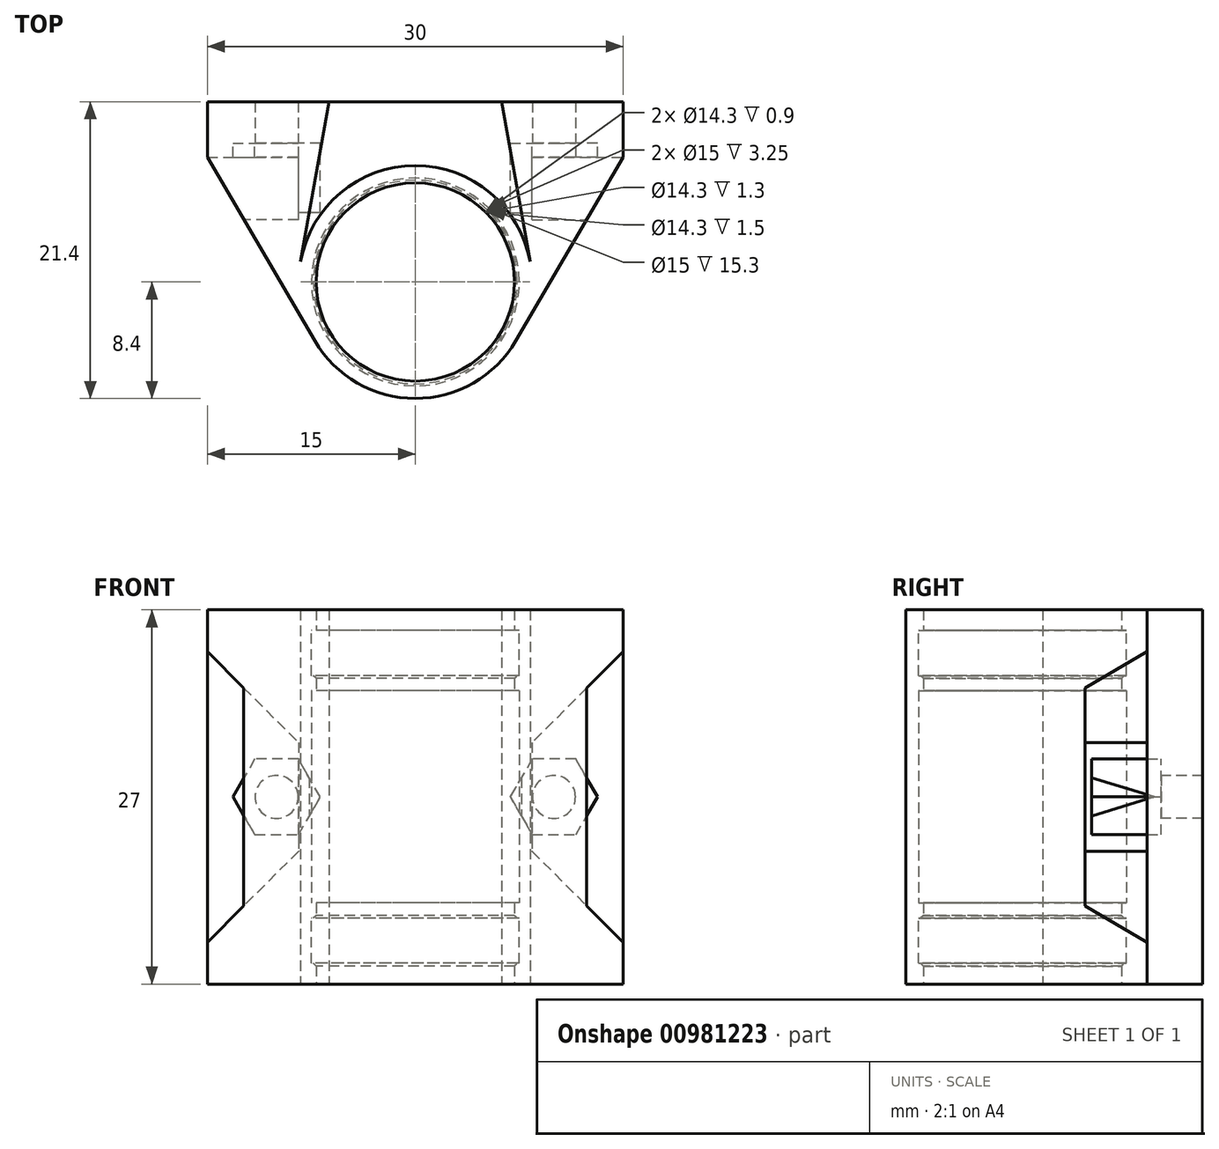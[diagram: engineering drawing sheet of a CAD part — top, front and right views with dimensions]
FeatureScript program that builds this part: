
annotation { "Feature Type Name" : "Feature", "Feature Type Description" : "" }
export const myFeature = defineFeature(function(context is Context, id is Id, definition is map)
    precondition{}
    {
        {
            var Q0;
            Q0=qCreatedBy(makeId("Top.planeOp"),FACE);
            var sketch = newSketch(context, id + "F0", { "sketchPlane" : qUnion([Q0])});
            skCircle(sketch, "E0", {"center": v(0, 0) * mm, "radius": 7.5 * mm});
            skLineSegment(sketch, "E1.top", {"start": v(-15, 9) * mm, "end": v(15, 9) * mm});
            skPoint(sketch, "E2", {"position": v(0, 9) * mm});
            skCircle(sketch, "E3", {"center": v(0, 0) * mm, "radius": 8.4 * mm});
            skCircle(sketch, "E4", {"center": v(0, 0) * mm, "radius": 7.15 * mm});
            skLineSegment(sketch, "E5", {"start": v(-8.27, 1.46) * mm, "end": v(-6.24, 13) * mm});
            skLineSegment(sketch, "E6", {"start": v(8.27, 1.46) * mm, "end": v(6.24, 13) * mm});
            skLineSegment(sketch, "E7", {"start": v(-15, 9) * mm, "end": v(-15, 13) * mm});
            skLineSegment(sketch, "E8", {"start": v(-15, 13) * mm, "end": v(15, 13) * mm});
            skLineSegment(sketch, "E9", {"start": v(15, 13) * mm, "end": v(15, 9) * mm});
            skLineSegment(sketch, "E10", {"start": v(-15, 9) * mm, "end": v(-7.25, -4.24) * mm});
            skLineSegment(sketch, "E11", {"start": v(15, 9) * mm, "end": v(7.25, -4.24) * mm});
            skLineSegment(sketch, "E12", {"start": v(9.73, 0) * mm, "end": v(-9.73, 0) * mm});
            skSolve(sketch);
        }
        {
            var Q0;
            {var subQ0=sQuery(id+"F0.wireOp",EDGE,"E5");var subQ1=sQuery(id+"F0.wireOp",EDGE,"E1.top");var subQ2=makeQuery(id+"F0.imprint","INTERSECT",VERTEX,{"derivedFrom":[subQ1,subQ0]});Q0=makeQuery(id+"F0.imprint","IMPRINT",FACE,{"disambiguationData":[TD([[makeQuery(id+"F0.imprint","IMPRINT",EDGE,{"disambiguationData":[TD([[subQ2,-1.0]])],"derivedFrom":subQ1}),1.0]])]});}
            var Q1;
            {var subQ0=sQuery(id+"F0.wireOp",EDGE,"E5");var subQ1=sQuery(id+"F0.wireOp",EDGE,"E1.top");var subQ2=makeQuery(id+"F0.imprint","INTERSECT",VERTEX,{"derivedFrom":[subQ1,subQ0]});Q1=makeQuery(id+"F0.imprint","IMPRINT",FACE,{"disambiguationData":[TD([[makeQuery(id+"F0.imprint","IMPRINT",EDGE,{"disambiguationData":[TD([[subQ2,-1.0]])],"derivedFrom":subQ1}),-1.0]])]});}
            var Q2;
            {var subQ2=sQuery(id+"F0.wireOp",EDGE,"E12");var subQ6=sQuery(id+"F0.wireOp",EDGE,"E0");var subQ7=makeQuery(id+"F0.imprint","INTERSECT",VERTEX,{"disambiguationData":[OD(0.0)],"derivedFrom":[subQ6,subQ2]});Q2=makeQuery(id+"F0.imprint","IMPRINT",FACE,{"disambiguationData":[TD([[makeQuery(id+"F0.imprint","IMPRINT",EDGE,{"disambiguationData":[TD([[subQ7,-1.0]])],"derivedFrom":subQ6}),-1.0]])]});}
            var Q3;
            {var subQ0=sQuery(id+"F0.wireOp",EDGE,"E12");var subQ1=sQuery(id+"F0.wireOp",EDGE,"E0");var subQ2=makeQuery(id+"F0.imprint","INTERSECT",VERTEX,{"disambiguationData":[OD(0.0)],"derivedFrom":[subQ1,subQ0]});Q3=makeQuery(id+"F0.imprint","IMPRINT",FACE,{"disambiguationData":[TD([[makeQuery(id+"F0.imprint","IMPRINT",EDGE,{"disambiguationData":[TD([[subQ2,-1.0]])],"derivedFrom":subQ1}),1.0]])]});}
            extrude(context, id + "F1", {"entities" : qUnion([Q0, Q1, Q2, Q3]), "endBound" : BoundingType.SYMMETRIC, "depth" : 27 * mm, "offsetDistance" : 25 * mm});
        }
        {
            var Q0;
            {var subQ3=sQuery(id+"F0.wireOp",EDGE,"E5");var subQ5=sQuery(id+"F0.wireOp",EDGE,"2ioF6rcV-CoDT-8IXQ-bcVH-CRvURSwV3O7U");var subQ6=makeQuery(id+"F0.imprint","INTERSECT",VERTEX,{"derivedFrom":[subQ3,subQ5]});Q0=makeQuery(id+"F0.imprint","IMPRINT",FACE,{"disambiguationData":[TD([[makeQuery(id+"F0.imprint","IMPRINT",EDGE,{"disambiguationData":[TD([[subQ6,1.0]])],"derivedFrom":subQ3}),1.0]])]});}
            var Q1;
            {var subQ1=sQuery(id+"F0.wireOp",EDGE,"E1.top");var subQ3=sQuery(id+"F0.wireOp",EDGE,"E5");var subQ4=makeQuery(id+"F0.imprint","INTERSECT",VERTEX,{"derivedFrom":[subQ1,subQ3]});Q1=makeQuery(id+"F0.imprint","IMPRINT",FACE,{"disambiguationData":[TD([[makeQuery(id+"F0.imprint","IMPRINT",EDGE,{"disambiguationData":[TD([[subQ4,1.0]])],"derivedFrom":subQ1}),-1.0]])]});}
            var Q2;
            {var subQ0=sQuery(id+"F0.wireOp",EDGE,"E12");var subQ6=sQuery(id+"F0.wireOp",EDGE,"E0");var subQ8=makeQuery(id+"F0.imprint","INTERSECT",VERTEX,{"disambiguationData":[OD(0.0)],"derivedFrom":[subQ6,subQ0]});Q2=makeQuery(id+"F0.imprint","IMPRINT",FACE,{"disambiguationData":[TD([[makeQuery(id+"F0.imprint","IMPRINT",EDGE,{"disambiguationData":[TD([[subQ8,1.0]])],"derivedFrom":subQ6}),-1.0]])]});}
            var Q3;
            {var subQ1=sQuery(id+"F0.wireOp",EDGE,"E3");var subQ3=sQuery(id+"F0.wireOp",EDGE,"E10");var subQ4=makeQuery(id+"F0.imprint","INTERSECT",VERTEX,{"derivedFrom":[subQ1,subQ3]});Q3=makeQuery(id+"F0.imprint","IMPRINT",FACE,{"disambiguationData":[TD([[makeQuery(id+"F0.imprint","IMPRINT",EDGE,{"disambiguationData":[TD([[subQ4,1.0]])],"derivedFrom":subQ3}),1.0]])]});}
            var Q4;
            {var subQ1=sQuery(id+"F0.wireOp",EDGE,"E3");var subQ3=sQuery(id+"F0.wireOp",EDGE,"E11");var subQ4=makeQuery(id+"F0.imprint","INTERSECT",VERTEX,{"derivedFrom":[subQ1,subQ3]});Q4=makeQuery(id+"F0.imprint","IMPRINT",FACE,{"disambiguationData":[TD([[makeQuery(id+"F0.imprint","IMPRINT",EDGE,{"disambiguationData":[TD([[subQ4,1.0]])],"derivedFrom":subQ3}),-1.0]])]});}
            var Q5;
            {var subQ1=sQuery(id+"F0.wireOp",EDGE,"E1.top");var subQ3=sQuery(id+"F0.wireOp",EDGE,"E6");var subQ4=makeQuery(id+"F0.imprint","INTERSECT",VERTEX,{"derivedFrom":[subQ1,subQ3]});Q5=makeQuery(id+"F0.imprint","IMPRINT",FACE,{"disambiguationData":[TD([[makeQuery(id+"F0.imprint","IMPRINT",EDGE,{"disambiguationData":[TD([[subQ4,-1.0]])],"derivedFrom":subQ1}),-1.0]])]});}
            var Q6;
            {var subQ3=sQuery(id+"F0.wireOp",EDGE,"E6");var subQ5=sQuery(id+"F0.wireOp",EDGE,"2ioF6rcV-CoDT-8IXQ-bcVH-CRvURSwV3O7U");var subQ6=makeQuery(id+"F0.imprint","INTERSECT",VERTEX,{"derivedFrom":[subQ3,subQ5]});Q6=makeQuery(id+"F0.imprint","IMPRINT",FACE,{"disambiguationData":[TD([[makeQuery(id+"F0.imprint","IMPRINT",EDGE,{"disambiguationData":[TD([[subQ6,1.0]])],"derivedFrom":subQ3}),-1.0]])]});}
            var Q7;
            {var subQ0=sQuery(id+"F0.wireOp",EDGE,"E12");var subQ1=sQuery(id+"F0.wireOp",EDGE,"E0");var subQ2=makeQuery(id+"F0.imprint","INTERSECT",VERTEX,{"disambiguationData":[OD(0.0)],"derivedFrom":[subQ1,subQ0]});Q7=makeQuery(id+"F0.imprint","IMPRINT",FACE,{"disambiguationData":[TD([[makeQuery(id+"F0.imprint","IMPRINT",EDGE,{"disambiguationData":[TD([[subQ2,1.0]])],"derivedFrom":subQ1}),1.0]])]});}
            extrude(context, id + "F2", {"entities" : qUnion([Q0, Q1, Q2, Q3, Q4, Q5, Q6, Q7]), "endBound" : BoundingType.SYMMETRIC, "depth" : 27 * mm, "offsetDistance" : 25 * mm});
        }
        {
            var Q0;
            {var subQ0=sQuery(id+"F0.wireOp",EDGE,"E12");var subQ1=sQuery(id+"F0.wireOp",EDGE,"E0");var subQ2=makeQuery(id+"F0.imprint","INTERSECT",VERTEX,{"disambiguationData":[OD(0.0)],"derivedFrom":[subQ1,subQ0]});Q0=makeQuery(id+"F0.imprint","IMPRINT",FACE,{"disambiguationData":[TD([[makeQuery(id+"F0.imprint","IMPRINT",EDGE,{"disambiguationData":[TD([[subQ2,-1.0]])],"derivedFrom":subQ1}),1.0]])]});}
            var Q1;
            {var subQ0=sQuery(id+"F0.wireOp",EDGE,"E12");var subQ1=sQuery(id+"F0.wireOp",EDGE,"E0");var subQ2=makeQuery(id+"F0.imprint","INTERSECT",VERTEX,{"disambiguationData":[OD(0.0)],"derivedFrom":[subQ1,subQ0]});Q1=makeQuery(id+"F0.imprint","IMPRINT",FACE,{"disambiguationData":[TD([[makeQuery(id+"F0.imprint","IMPRINT",EDGE,{"disambiguationData":[TD([[subQ2,1.0]])],"derivedFrom":subQ1}),1.0]])]});}
            extrude(context, id + "F3", {"entities" : qUnion([Q0, Q1]), "operationType" : NewBodyOperationType.REMOVE, "endBound" : BoundingType.SYMMETRIC, "oppositeDirection" : true, "depth" : 24 * mm, "offsetDistance" : 25 * mm});
        }
        {
            var Q0;
            {var subQ0=sQuery(id+"F0.wireOp",EDGE,"E12");var subQ1=sQuery(id+"F0.wireOp",EDGE,"E0");var subQ2=makeQuery(id+"F0.imprint","INTERSECT",VERTEX,{"disambiguationData":[OD(0.0)],"derivedFrom":[subQ1,subQ0]});Q0=makeQuery(id+"F0.imprint","IMPRINT",FACE,{"disambiguationData":[TD([[makeQuery(id+"F0.imprint","IMPRINT",EDGE,{"disambiguationData":[TD([[subQ2,-1.0]])],"derivedFrom":subQ1}),1.0]])]});}
            extrude(context, id + "F4", {"entities" : qUnion([Q0]), "operationType" : NewBodyOperationType.ADD, "endBound" : BoundingType.SYMMETRIC, "depth" : 17.5 * mm, "offsetDistance" : 25 * mm});
        }
        {
            var Q0;
            {var subQ0=sQuery(id+"F0.wireOp",EDGE,"E12");var subQ1=sQuery(id+"F0.wireOp",EDGE,"E0");var subQ2=makeQuery(id+"F0.imprint","INTERSECT",VERTEX,{"disambiguationData":[OD(0.0)],"derivedFrom":[subQ1,subQ0]});Q0=makeQuery(id+"F0.imprint","IMPRINT",FACE,{"disambiguationData":[TD([[makeQuery(id+"F0.imprint","IMPRINT",EDGE,{"disambiguationData":[TD([[subQ2,1.0]])],"derivedFrom":subQ1}),1.0]])]});}
            extrude(context, id + "F5", {"entities" : qUnion([Q0]), "operationType" : NewBodyOperationType.ADD, "endBound" : BoundingType.SYMMETRIC, "depth" : 17.5 * mm, "offsetDistance" : 25 * mm});
        }
        {
            var Q0;
            {var subQ0=sQuery(id+"F0.wireOp",EDGE,"E12");var subQ1=sQuery(id+"F0.wireOp",EDGE,"E0");var subQ2=makeQuery(id+"F0.imprint","INTERSECT",VERTEX,{"disambiguationData":[OD(0.0)],"derivedFrom":[subQ1,subQ0]});Q0=makeQuery(id+"F0.imprint","IMPRINT",FACE,{"disambiguationData":[TD([[makeQuery(id+"F0.imprint","IMPRINT",EDGE,{"disambiguationData":[TD([[subQ2,-1.0]])],"derivedFrom":subQ1}),1.0]])]});}
            var Q1;
            {var subQ0=sQuery(id+"F0.wireOp",EDGE,"E12");var subQ1=sQuery(id+"F0.wireOp",EDGE,"E0");var subQ2=makeQuery(id+"F0.imprint","INTERSECT",VERTEX,{"disambiguationData":[OD(0.0)],"derivedFrom":[subQ1,subQ0]});Q1=makeQuery(id+"F0.imprint","IMPRINT",FACE,{"disambiguationData":[TD([[makeQuery(id+"F0.imprint","IMPRINT",EDGE,{"disambiguationData":[TD([[subQ2,1.0]])],"derivedFrom":subQ1}),1.0]])]});}
            var Q2;
            Q2=makeQuery(id+"F4.opExtrude","CAP_FACE",FACE,{"disambiguationData":[OSD([sQuery(id+"F0.wireOp",EDGE,"E0"),sQuery(id+"F0.wireOp",EDGE,"E4"),sQuery(id+"F0.wireOp",EDGE,"OyqxnQTL-80hJ-Tre8-0LPI-5BT4BykeZ9OB"),sQuery(id+"F0.wireOp",EDGE,"toQEOSAH-RIUy-FKcM-AJDC-1LW4buzCWPbQ")])],"isStart":false});
            var Q3;
            Q3=makeQuery(id+"F4.opExtrude","CAP_FACE",FACE,{"disambiguationData":[OSD([sQuery(id+"F0.wireOp",EDGE,"E0"),sQuery(id+"F0.wireOp",EDGE,"E4"),sQuery(id+"F0.wireOp",EDGE,"OyqxnQTL-80hJ-Tre8-0LPI-5BT4BykeZ9OB"),sQuery(id+"F0.wireOp",EDGE,"toQEOSAH-RIUy-FKcM-AJDC-1LW4buzCWPbQ")])],"isStart":true});
            extrude(context, id + "F6", {"entities" : qUnion([Q0, Q1]), "operationType" : NewBodyOperationType.REMOVE, "endBound" : BoundingType.UP_TO_SURFACE, "depth" : 15 * mm, "endBoundEntityFace" : qUnion([Q2]), "hasOffset" : true, "offsetDistance" : 1.1 * mm, "hasSecondDirection" : true, "secondDirectionBound" : SecondDirectionBoundingType.UP_TO_SURFACE, "secondDirectionOppositeDirection" : true, "secondDirectionDepth" : 25 * mm, "secondDirectionBoundEntityFace" : qUnion([Q3]), "hasSecondDirectionOffset" : true, "secondDirectionOffsetDistance" : 1.1 * mm});
        }
        {
            var Q0;
            Q0=makeQuery(id+"F1.opExtrude","SWEPT_FACE",FACE,{"disambiguationData":[OSD([sQuery(id+"F0.wireOp",EDGE,"E8")])]});
            cPlane(context, id + "F7", {"entities" : qUnion([Q0]), "cplaneType" : CPlaneType.OFFSET, "offset" : 4 * mm, "oppositeDirection" : true, "width" : 150 * mm, "height" : 150 * mm});
        }
        {
            var Q0;
            Q0=qCreatedBy(id+"F7.planeOp",FACE);
            var sketch = newSketch(context, id + "F8", { "sketchPlane" : qUnion([Q0])});
            skCircle(sketch, "E13", {"center": v(-10, 0) * mm, "radius": 1.55 * mm});
            skCircle(sketch, "E14", {"center": v(10, 0) * mm, "radius": 1.55 * mm});
            skCircle(sketch, "E15.cCircle", {"center": v(-10, 0) * mm, "radius": 3.15 * mm, "construction": true});
            skLineSegment(sketch, "E15.0", {"start": v(-6.85, 0) * mm, "end": v(-8.43, -2.73) * mm});
            skLineSegment(sketch, "E15.1", {"start": v(-8.43, -2.73) * mm, "end": v(-11.58, -2.73) * mm});
            skLineSegment(sketch, "E15.2", {"start": v(-11.58, -2.73) * mm, "end": v(-13.15, 0) * mm});
            skLineSegment(sketch, "E15.3", {"start": v(-13.15, 0) * mm, "end": v(-11.58, 2.73) * mm});
            skLineSegment(sketch, "E15.4", {"start": v(-11.58, 2.73) * mm, "end": v(-8.43, 2.73) * mm});
            skLineSegment(sketch, "E15.5", {"start": v(-8.43, 2.73) * mm, "end": v(-6.85, 0) * mm});
            skCircle(sketch, "E16.cCircle", {"center": v(10, 0) * mm, "radius": 3.15 * mm, "construction": true});
            skLineSegment(sketch, "E16.0", {"start": v(6.85, 0) * mm, "end": v(8.43, 2.73) * mm});
            skLineSegment(sketch, "E16.1", {"start": v(8.43, 2.73) * mm, "end": v(11.58, 2.73) * mm});
            skLineSegment(sketch, "E16.2", {"start": v(11.58, 2.73) * mm, "end": v(13.15, 0) * mm});
            skLineSegment(sketch, "E16.3", {"start": v(13.15, 0) * mm, "end": v(11.58, -2.73) * mm});
            skLineSegment(sketch, "E16.4", {"start": v(11.58, -2.73) * mm, "end": v(8.43, -2.73) * mm});
            skLineSegment(sketch, "E16.5", {"start": v(8.43, -2.73) * mm, "end": v(6.85, 0) * mm});
            skLineSegment(sketch, "E17", {"start": v(-15, -10.5) * mm, "end": v(-15, 10.5) * mm});
            skLineSegment(sketch, "E18", {"start": v(-15, 10.5) * mm, "end": v(-8.43, 3.92) * mm});
            skLineSegment(sketch, "E19", {"start": v(-8.43, 3.92) * mm, "end": v(-8.43, -3.92) * mm});
            skLineSegment(sketch, "E20", {"start": v(-8.43, -3.92) * mm, "end": v(-15, -10.5) * mm});
            skLineSegment(sketch, "E21", {"start": v(15, 10.5) * mm, "end": v(8.43, 3.92) * mm});
            skLineSegment(sketch, "E22", {"start": v(8.43, 3.92) * mm, "end": v(8.43, -3.92) * mm});
            skLineSegment(sketch, "E23", {"start": v(8.43, -3.92) * mm, "end": v(15, -10.5) * mm});
            skLineSegment(sketch, "E24", {"start": v(15, -10.5) * mm, "end": v(15, 10.5) * mm});
            skPoint(sketch, "E25", {"position": v(-15, 0) * mm});
            skSolve(sketch);
        }
        {
            var Q0;
            {var subQ4=sQuery(id+"F8.wireOp",EDGE,"E15.2");Q0=makeQuery(id+"F8.imprint","IMPRINT",FACE,{"disambiguationData":[TD([[makeQuery(id+"F8.imprint","IMPRINT",EDGE,{"derivedFrom":subQ4}),1.0]])]});}
            var Q1;
            {var subQ5=sQuery(id+"F8.wireOp",EDGE,"E16.2");Q1=makeQuery(id+"F8.imprint","IMPRINT",FACE,{"disambiguationData":[TD([[makeQuery(id+"F8.imprint","IMPRINT",EDGE,{"derivedFrom":subQ5}),1.0]])]});}
            var Q2;
            {var subQ1=sQuery(id+"F8.wireOp",EDGE,"E16.2");Q2=makeQuery(id+"F8.imprint","IMPRINT",FACE,{"disambiguationData":[TD([[makeQuery(id+"F8.imprint","IMPRINT",EDGE,{"derivedFrom":subQ1}),-1.0]])]});}
            var Q3;
            {var subQ0=sQuery(id+"F8.wireOp",EDGE,"E22");var subQ1=sQuery(id+"F8.wireOp",EDGE,"E14");var subQ2=makeQuery(id+"F8.imprint","INTERSECT",VERTEX,{"disambiguationData":[OD(0.0)],"derivedFrom":[subQ1,subQ0]});Q3=makeQuery(id+"F8.imprint","IMPRINT",FACE,{"disambiguationData":[TD([[makeQuery(id+"F8.imprint","IMPRINT",EDGE,{"disambiguationData":[TD([[subQ2,1.0]])],"derivedFrom":subQ1}),1.0]])]});}
            var Q4;
            {var subQ1=sQuery(id+"F8.wireOp",EDGE,"E15.2");Q4=makeQuery(id+"F8.imprint","IMPRINT",FACE,{"disambiguationData":[TD([[makeQuery(id+"F8.imprint","IMPRINT",EDGE,{"derivedFrom":subQ1}),-1.0]])]});}
            var Q5;
            {var subQ0=sQuery(id+"F8.wireOp",EDGE,"E19");var subQ1=sQuery(id+"F8.wireOp",EDGE,"E13");var subQ2=makeQuery(id+"F8.imprint","INTERSECT",VERTEX,{"disambiguationData":[OD(0.0)],"derivedFrom":[subQ1,subQ0]});Q5=makeQuery(id+"F8.imprint","IMPRINT",FACE,{"disambiguationData":[TD([[makeQuery(id+"F8.imprint","IMPRINT",EDGE,{"disambiguationData":[TD([[subQ2,-1.0]])],"derivedFrom":subQ1}),1.0]])]});}
            extrude(context, id + "F9", {"entities" : qUnion([Q0, Q1, Q2, Q3, Q4, Q5]), "operationType" : NewBodyOperationType.REMOVE, "oppositeDirection" : true, "depth" : 4.5 * mm, "offsetDistance" : 25 * mm});
        }
        {
            var Q0;
            {var subQ1=sQuery(id+"F8.wireOp",EDGE,"E15.2");Q0=makeQuery(id+"F8.imprint","IMPRINT",FACE,{"disambiguationData":[TD([[makeQuery(id+"F8.imprint","IMPRINT",EDGE,{"derivedFrom":subQ1}),-1.0]])]});}
            var Q1;
            {var subQ5=sQuery(id+"F8.wireOp",EDGE,"E15.0");Q1=makeQuery(id+"F8.imprint","IMPRINT",FACE,{"disambiguationData":[TD([[makeQuery(id+"F8.imprint","IMPRINT",EDGE,{"derivedFrom":subQ5}),-1.0]])]});}
            var Q2;
            {var subQ0=sQuery(id+"F8.wireOp",EDGE,"E19");var subQ1=sQuery(id+"F8.wireOp",EDGE,"E13");var subQ2=makeQuery(id+"F8.imprint","INTERSECT",VERTEX,{"disambiguationData":[OD(0.0)],"derivedFrom":[subQ1,subQ0]});Q2=makeQuery(id+"F8.imprint","IMPRINT",FACE,{"disambiguationData":[TD([[makeQuery(id+"F8.imprint","IMPRINT",EDGE,{"disambiguationData":[TD([[subQ2,1.0]])],"derivedFrom":subQ1}),1.0]])]});}
            var Q3;
            {var subQ1=sQuery(id+"F8.wireOp",EDGE,"E16.2");Q3=makeQuery(id+"F8.imprint","IMPRINT",FACE,{"disambiguationData":[TD([[makeQuery(id+"F8.imprint","IMPRINT",EDGE,{"derivedFrom":subQ1}),-1.0]])]});}
            var Q4;
            {var subQ0=sQuery(id+"F8.wireOp",EDGE,"E22");var subQ1=sQuery(id+"F8.wireOp",EDGE,"E14");var subQ2=makeQuery(id+"F8.imprint","INTERSECT",VERTEX,{"disambiguationData":[OD(0.0)],"derivedFrom":[subQ1,subQ0]});Q4=makeQuery(id+"F8.imprint","IMPRINT",FACE,{"disambiguationData":[TD([[makeQuery(id+"F8.imprint","IMPRINT",EDGE,{"disambiguationData":[TD([[subQ2,-1.0]])],"derivedFrom":subQ1}),1.0]])]});}
            var Q5;
            {var subQ5=sQuery(id+"F8.wireOp",EDGE,"E16.0");Q5=makeQuery(id+"F8.imprint","IMPRINT",FACE,{"disambiguationData":[TD([[makeQuery(id+"F8.imprint","IMPRINT",EDGE,{"derivedFrom":subQ5}),-1.0]])]});}
            extrude(context, id + "F10", {"entities" : qUnion([Q0, Q1, Q2, Q3, Q4, Q5]), "operationType" : NewBodyOperationType.REMOVE, "oppositeDirection" : true, "depth" : 4 * mm, "offsetDistance" : 25 * mm, "hasSecondDirection" : true, "secondDirectionOppositeDirection" : false, "secondDirectionDepth" : 1 * mm});
        }
        {
            var Q0;
            Q0=makeQuery(id+"F8.imprint","IMPRINT",FACE,{"disambiguationData":[TD([[makeQuery(id+"F8.imprint","IMPRINT",EDGE,{"derivedFrom":sQuery(id+"F8.wireOp",EDGE,"E13")}),1.0]])]});
            var Q1;
            Q1=makeQuery(id+"F8.imprint","IMPRINT",FACE,{"disambiguationData":[TD([[makeQuery(id+"F8.imprint","IMPRINT",EDGE,{"derivedFrom":sQuery(id+"F8.wireOp",EDGE,"E14")}),1.0]])]});
            extrude(context, id + "F11", {"entities" : qUnion([Q0, Q1]), "operationType" : NewBodyOperationType.REMOVE, "endBound" : BoundingType.THROUGH_ALL, "depth" : 25 * mm, "offsetDistance" : 25 * mm});
        }
        {
            var Q0;
            Q0=makeQuery(id+"F4.opExtrude","CAP_EDGE",EDGE,{"disambiguationData":[OSD([sQuery(id+"F0.wireOp",EDGE,"E4")])],"isStart":true});
            var Q1;
            {var subQ0=sQuery(id+"F0.wireOp",EDGE,"E4");var subQ1=sQuery(id+"F0.wireOp",EDGE,"E12");var subQ2=sQuery(id+"F0.wireOp",EDGE,"E0");var subQ3=makeQuery(id+"F0.imprint","INTERSECT",VERTEX,{"disambiguationData":[OD(0.0)],"derivedFrom":[subQ0,subQ1]});Q1=makeQuery(id+"F6.boolean.opBoolean","COPY",EDGE,{"disambiguationData":[topologyDisambiguationEdgeConnected([makeQuery(id+"F4.opExtrude","SWEPT_FACE",FACE,{"disambiguationData":[OSD([subQ0])]})])],"derivedFrom":makeQuery(id+"F6.opExtrude","TWEAK_EDGE",EDGE,{"derivedFrom":[makeQuery(id+"F0.imprint","IMPRINT",EDGE,{"disambiguationData":[TD([[subQ3,-1.0]])],"derivedFrom":subQ0}),makeQuery(id+"F0.imprint","IMPRINT",EDGE,{"disambiguationData":[TD([[subQ3,1.0]])],"derivedFrom":subQ0}),makeQuery(id+"F4.opExtrude","CAP_FACE",FACE,{"disambiguationData":[OSD([subQ2,subQ0,subQ1])],"isStart":true})]})});}
            var Q2;
            {var subQ0=sQuery(id+"F0.wireOp",EDGE,"E4");Q2=makeQuery(id+"F3.boolean.opBoolean","COPY",EDGE,{"disambiguationData":[topologyDisambiguationEdgeConnected([makeQuery(id+"F1.opExtrude","SWEPT_FACE",FACE,{"disambiguationData":[OSD([subQ0])]})])],"derivedFrom":makeQuery(id+"F3.opExtrude","CAP_EDGE",EDGE,{"disambiguationData":[OSD([subQ0])],"isStart":false})});}
            var Q3;
            {var subQ0=sQuery(id+"F0.wireOp",EDGE,"E4");var subQ1=sQuery(id+"F0.wireOp",EDGE,"E12");var subQ2=sQuery(id+"F0.wireOp",EDGE,"E0");var subQ3=makeQuery(id+"F0.imprint","INTERSECT",VERTEX,{"disambiguationData":[OD(0.0)],"derivedFrom":[subQ0,subQ1]});Q3=makeQuery(id+"F6.boolean.opBoolean","COPY",EDGE,{"disambiguationData":[topologyDisambiguationEdgeConnected([makeQuery(id+"F4.opExtrude","SWEPT_FACE",FACE,{"disambiguationData":[OSD([subQ0])]})])],"derivedFrom":makeQuery(id+"F6.opExtrude","TWEAK_EDGE",EDGE,{"derivedFrom":[makeQuery(id+"F0.imprint","IMPRINT",EDGE,{"disambiguationData":[TD([[subQ3,-1.0]])],"derivedFrom":subQ0}),makeQuery(id+"F0.imprint","IMPRINT",EDGE,{"disambiguationData":[TD([[subQ3,1.0]])],"derivedFrom":subQ0}),makeQuery(id+"F4.opExtrude","CAP_FACE",FACE,{"disambiguationData":[OSD([subQ2,subQ0,subQ1])],"isStart":false})]})});}
            var Q4;
            Q4=makeQuery(id+"F4.opExtrude","CAP_EDGE",EDGE,{"disambiguationData":[OSD([sQuery(id+"F0.wireOp",EDGE,"E4")])],"isStart":false});
            var Q5;
            {var subQ0=sQuery(id+"F0.wireOp",EDGE,"E4");Q5=makeQuery(id+"F3.boolean.opBoolean","COPY",EDGE,{"disambiguationData":[topologyDisambiguationEdgeConnected([makeQuery(id+"F1.opExtrude","SWEPT_FACE",FACE,{"disambiguationData":[OSD([subQ0])]})])],"derivedFrom":makeQuery(id+"F3.opExtrude","CAP_EDGE",EDGE,{"disambiguationData":[OSD([subQ0])],"isStart":true})});}
            var Q6;
            {var subQ0=sQuery(id+"F0.wireOp",EDGE,"E4");Q6=makeQuery(id+"F3.boolean.opBoolean","COPY",EDGE,{"disambiguationData":[topologyDisambiguationEdgeConnected([makeQuery(id+"F2.opExtrude","SWEPT_FACE",FACE,{"disambiguationData":[OSD([subQ0])]})])],"derivedFrom":makeQuery(id+"F3.opExtrude","CAP_EDGE",EDGE,{"disambiguationData":[OSD([subQ0])],"isStart":false})});}
            var Q7;
            Q7=makeQuery(id+"F5.opExtrude","CAP_EDGE",EDGE,{"disambiguationData":[OSD([sQuery(id+"F0.wireOp",EDGE,"E4")])],"isStart":true});
            var Q8;
            {var subQ0=sQuery(id+"F0.wireOp",EDGE,"E4");var subQ1=sQuery(id+"F0.wireOp",EDGE,"E12");var subQ2=sQuery(id+"F0.wireOp",EDGE,"E0");var subQ3=makeQuery(id+"F0.imprint","INTERSECT",VERTEX,{"disambiguationData":[OD(0.0)],"derivedFrom":[subQ0,subQ1]});Q8=makeQuery(id+"F6.boolean.opBoolean","COPY",EDGE,{"disambiguationData":[topologyDisambiguationEdgeConnected([makeQuery(id+"F5.opExtrude","SWEPT_FACE",FACE,{"disambiguationData":[OSD([subQ0])]})])],"derivedFrom":makeQuery(id+"F6.opExtrude","TWEAK_EDGE",EDGE,{"derivedFrom":[makeQuery(id+"F0.imprint","IMPRINT",EDGE,{"disambiguationData":[TD([[subQ3,-1.0]])],"derivedFrom":subQ0}),makeQuery(id+"F0.imprint","IMPRINT",EDGE,{"disambiguationData":[TD([[subQ3,1.0]])],"derivedFrom":subQ0}),makeQuery(id+"F4.opExtrude","CAP_FACE",FACE,{"disambiguationData":[OSD([subQ2,subQ0,subQ1])],"isStart":true})]})});}
            var Q9;
            {var subQ0=sQuery(id+"F0.wireOp",EDGE,"E4");var subQ1=sQuery(id+"F0.wireOp",EDGE,"E12");var subQ2=sQuery(id+"F0.wireOp",EDGE,"E0");var subQ3=makeQuery(id+"F0.imprint","INTERSECT",VERTEX,{"disambiguationData":[OD(0.0)],"derivedFrom":[subQ0,subQ1]});Q9=makeQuery(id+"F6.boolean.opBoolean","COPY",EDGE,{"disambiguationData":[topologyDisambiguationEdgeConnected([makeQuery(id+"F5.opExtrude","SWEPT_FACE",FACE,{"disambiguationData":[OSD([subQ0])]})])],"derivedFrom":makeQuery(id+"F6.opExtrude","TWEAK_EDGE",EDGE,{"derivedFrom":[makeQuery(id+"F0.imprint","IMPRINT",EDGE,{"disambiguationData":[TD([[subQ3,-1.0]])],"derivedFrom":subQ0}),makeQuery(id+"F0.imprint","IMPRINT",EDGE,{"disambiguationData":[TD([[subQ3,1.0]])],"derivedFrom":subQ0}),makeQuery(id+"F4.opExtrude","CAP_FACE",FACE,{"disambiguationData":[OSD([subQ2,subQ0,subQ1])],"isStart":false})]})});}
            var Q10;
            Q10=makeQuery(id+"F5.opExtrude","CAP_EDGE",EDGE,{"disambiguationData":[OSD([sQuery(id+"F0.wireOp",EDGE,"E4")])],"isStart":false});
            var Q11;
            {var subQ0=sQuery(id+"F0.wireOp",EDGE,"E4");Q11=makeQuery(id+"F3.boolean.opBoolean","COPY",EDGE,{"disambiguationData":[topologyDisambiguationEdgeConnected([makeQuery(id+"F2.opExtrude","SWEPT_FACE",FACE,{"disambiguationData":[OSD([subQ0])]})])],"derivedFrom":makeQuery(id+"F3.opExtrude","CAP_EDGE",EDGE,{"disambiguationData":[OSD([subQ0])],"isStart":true})});}
            chamfer(context, id + "F12", {"entities" : qUnion([Q0, Q1, Q2, Q3, Q4, Q5, Q6, Q7, Q8, Q9, Q10, Q11]), "width" : .2 * mm, "tangentPropagation" : true});
        }
    });
